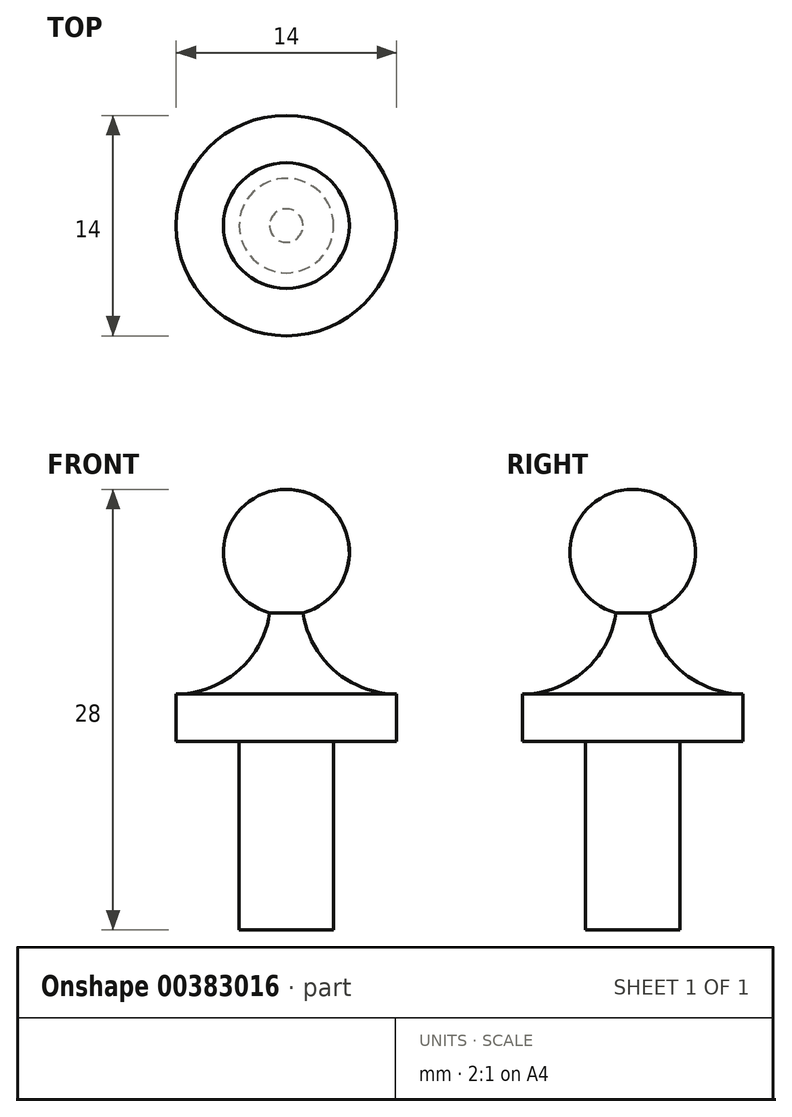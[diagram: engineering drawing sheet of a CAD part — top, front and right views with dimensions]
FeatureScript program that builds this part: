
annotation { "Feature Type Name" : "Feature", "Feature Type Description" : "" }
export const myFeature = defineFeature(function(context is Context, id is Id, definition is map)
    precondition{}
    {
        {
            var Q0;
            Q0=qCreatedBy(makeId("Front.planeOp"),FACE);
            var sketch = newSketch(context, id + "F0", { "sketchPlane" : qUnion([Q0])});
            skLineSegment(sketch, "E0", {"start": v(0, 12) * mm, "end": v(0, -25.56) * mm, "construction": true});
            skLineSegment(sketch, "E1", {"start": v(-7, 0) * mm, "end": v(-7, 3) * mm});
            skLineSegment(sketch, "E2", {"start": v(-7, 0) * mm, "end": v(-3, 0) * mm});
            skLineSegment(sketch, "E3", {"start": v(-3, 0) * mm, "end": v(-3, -12) * mm});
            skLineSegment(sketch, "E4", {"start": v(-3, -12) * mm, "end": v(0, -12) * mm});
            skArc(sketch, "E5", {"start": v(0, 16) * mm, "mid": v(-3.97, 12.5) * mm, "end": v(-1, 8.13) * mm});
            skLineSegment(sketch, "E6", {"start": v(-1, 11.67) * mm, "end": v(-1, 6.33) * mm, "construction": true});
            skArc(sketch, "E7", {"start": v(-7, 3) * mm, "mid": v(-3.07, 4.46) * mm, "end": v(-1.06, 8.14) * mm});
            skPoint(sketch, "E8", {"position": v(-1.06, 8.14) * mm});
            skPoint(sketch, "E9", {"position": v(-3.57, 7.21) * mm});
            skPoint(sketch, "E10.orphan", {"position": v(-1, 9) * mm});
            skLineSegment(sketch, "E11", {"start": v(0, -25.56) * mm, "end": v(0, 25.22) * mm, "construction": true});
            skLineSegment(sketch, "E12", {"start": v(0, 16) * mm, "end": v(0, -12) * mm});
            skSolve(sketch);
        }
        {
            var Q0;
            Q0 = qSketchRegion(id + "F0", true);
            var Q1;
            Q1=sQuery(id+"F0.wireOp",EDGE,"E11");
            revolve(context, id + "F1", {"surfaceOperationType" : NewSurfaceOperationType.NEW, "entities" : qUnion([Q0]), "axis" : qUnion([Q1]), "revolveType" : RevolveType.FULL});
        }
    });
